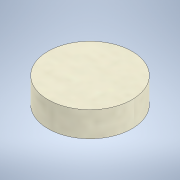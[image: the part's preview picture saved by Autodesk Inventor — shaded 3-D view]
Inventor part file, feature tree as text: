
AUTODESK INVENTOR PART (.ipt)
format: ipt  version: 2021 (Build 250183000, 183)  size: 99,840 bytes
history: native  units: mm
features: extrude x1, sketch x1
ambient origin geometry x8: Origin, YZ Plane, XZ Plane, XY Plane, X Axis, Y Axis, Z Axis, Center Point
bodies: Solid1 (feature_tree)
feature tree (2):
  extrude  "Extrusion1"  Depth=9.45mm TaperAngle=0.0deg
  sketch  "Sketch1"  dims[d0=31.5mm d1=9.45mm d2=0.0mm]
